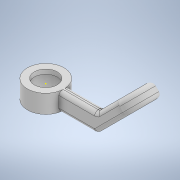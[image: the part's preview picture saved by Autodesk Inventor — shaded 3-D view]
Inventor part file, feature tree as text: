
AUTODESK INVENTOR PART (.ipt)
format: ipt  version: 2022 (Build 260153000, 153)  size: 209,408 bytes
history: native  units: mm
features: sketch x8, extrude x7, fillet x2, other x1
ambient origin geometry x8: Origin, YZ Plane, XZ Plane, XY Plane, X Axis, Y Axis, Z Axis, Center Point
bodies: Body1 (feature_tree)
feature tree (18):
  other  "Bryła1"
  extrude  "Wyciągnięcie proste1"  Depth=40.0mm
  extrude  "Wyciągnięcie proste2"  Depth=20.0mm TaperAngle=0.0deg
  extrude  "Wyciągnięcie proste3"  Depth=20.0mm
  extrude  "Wyciągnięcie proste4"  TaperAngle=45.0deg  [1 undecoded]
  extrude  "Wyciągnięcie proste5"  Depth=134.0mm
  fillet  "Zaokrąglenie2"  Radius=60.0mm
  extrude  "Wyciągnięcie proste6"  Depth=10.0mm TaperAngle=0.0deg
  extrude  "Wyciągnięcie proste7"  Depth=22.0mm
  fillet  "Zaokrąglenie3"  Radius=5.0mm
  sketch  "Szkic8"
  sketch  "Szkic1"
  sketch  "Szkic2"
  sketch  "Szkic3"
  sketch  "Szkic4"
  sketch  "Szkic5"
  sketch  "Szkic6"
  sketch  "Szkic7"
note: 1 required parameter value undecoded (feature->parameter linkage not recoverable at this tier; creation-order binding heuristic only, values carry confidence <= 0.55)
